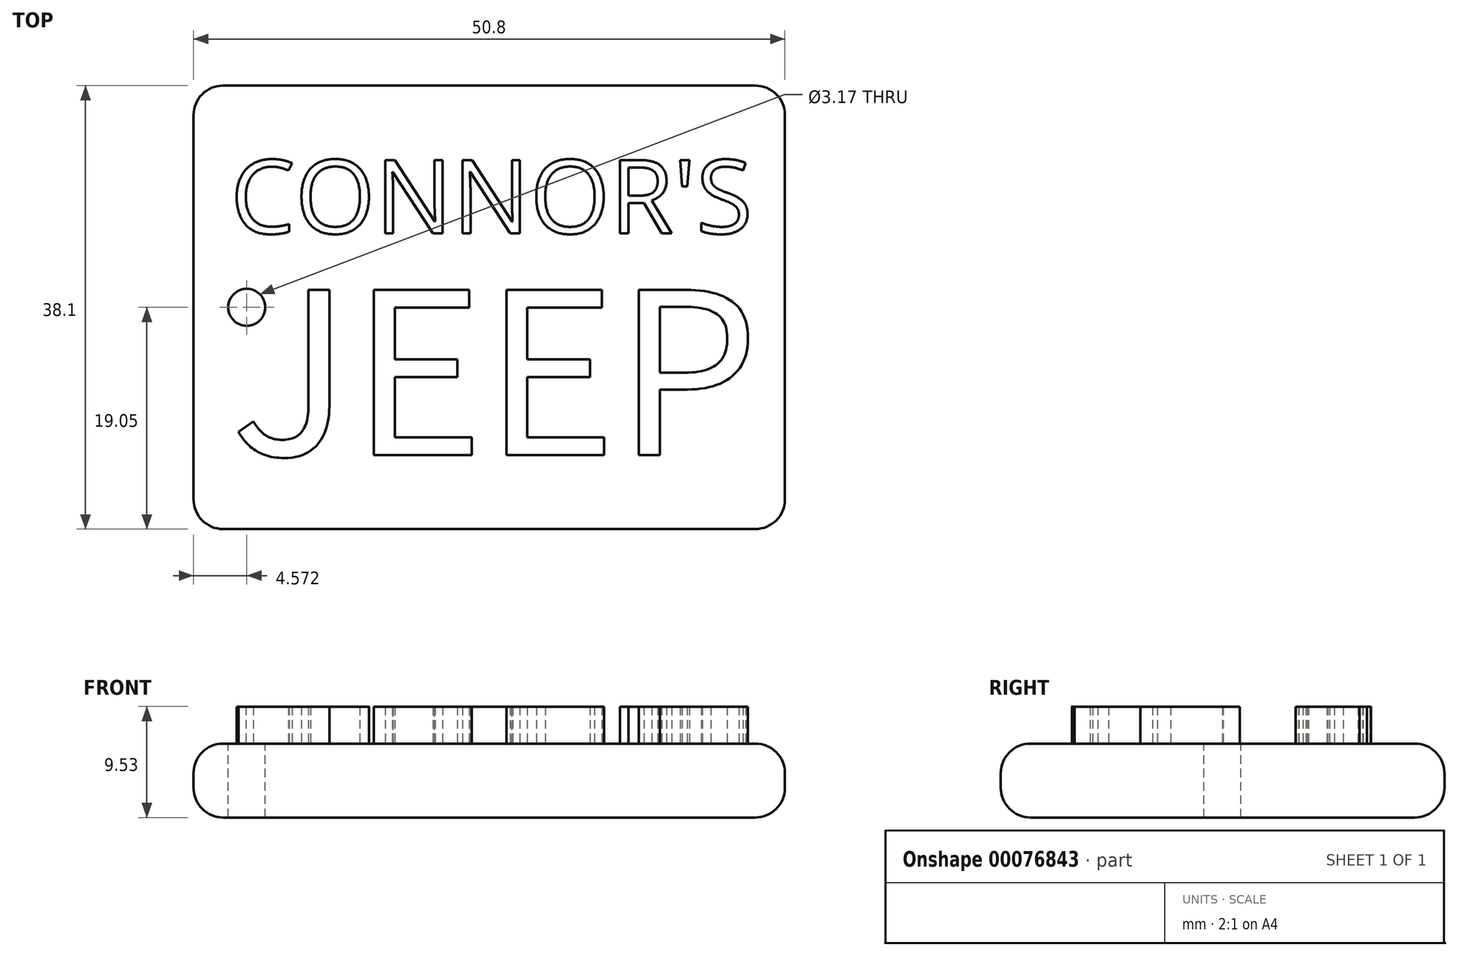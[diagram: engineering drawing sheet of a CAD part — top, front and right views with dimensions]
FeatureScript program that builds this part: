
annotation { "Feature Type Name" : "Feature", "Feature Type Description" : "" }
export const myFeature = defineFeature(function(context is Context, id is Id, definition is map)
    precondition{}
    {
        {
            var Q0;
            Q0=qCreatedBy(makeId("Top.planeOp"),FACE);
            var sketch = newSketch(context, id + "F0", { "sketchPlane" : qUnion([Q0])});
            skLineSegment(sketch, "E0.bottom", {"start": v(-31.75, 25.4) * mm, "end": v(19.05, 25.4) * mm});
            skLineSegment(sketch, "E0.top", {"start": v(-31.75, -12.7) * mm, "end": v(19.05, -12.7) * mm});
            skLineSegment(sketch, "E0.left", {"start": v(-31.75, 25.4) * mm, "end": v(-31.75, -12.7) * mm});
            skLineSegment(sketch, "E0.right", {"start": v(19.05, 25.4) * mm, "end": v(19.05, -12.7) * mm});
            skSolve(sketch);
        }
        {
            var Q0;
            Q0 = qSketchRegion(id + "F0", true);
            extrude(context, id + "F1", {"entities" : qUnion([Q0]), "depth" : 6.35 * mm});
        }
        {
            var Q0;
            Q0=makeQuery(id+"F1.opExtrude","CAP_FACE",FACE,{"disambiguationData":[OSD([sQuery(id+"F0.wireOp",EDGE,"E0.bottom"),sQuery(id+"F0.wireOp",EDGE,"E0.top"),sQuery(id+"F0.wireOp",EDGE,"E0.left"),sQuery(id+"F0.wireOp",EDGE,"E0.right")])],"isStart":false});
            var sketch = newSketch(context, id + "F2", { "sketchPlane" : qUnion([Q0])});
            skText(sketch, "E1", { "text": "JEEP", "fontName": "NotoSansCJKtc-Regular.otf"});
            const initialGuessF2  = {"E1": [-0.02857, -0.00635, 1, 0, 0.01394]};
            skSetInitialGuess(sketch, initialGuessF2);
            skSolve(sketch);
        }
        {
            var Q0;
            Q0 = qSketchRegion(id + "F2", true);
            extrude(context, id + "F3", {"entities" : qUnion([Q0]), "operationType" : NewBodyOperationType.ADD, "depth" : 3.17 * mm});
        }
        {
            var Q0;
            {var subQ0=sQuery(id+"F0.wireOp",EDGE,"E0.bottom");var subQ1=sQuery(id+"F0.wireOp",EDGE,"E0.right");var subQ2=sQuery(id+"F0.wireOp",EDGE,"E0.top");var subQ3=sQuery(id+"F0.wireOp",EDGE,"E0.left");Q0=makeQuery(id+"F3.boolean.opBoolean","SPLIT",FACE,{"disambiguationData":[TD([makeQuery(id+"F1.opExtrude","SWEPT_FACE",FACE,{"disambiguationData":[OSD([subQ0])]})])],"derivedFrom":makeQuery(id+"F1.opExtrude","CAP_FACE",FACE,{"disambiguationData":[OSD([subQ0,subQ2,subQ3,subQ1])],"isStart":false})});}
            var sketch = newSketch(context, id + "F4", { "sketchPlane" : qUnion([Q0])});
            skText(sketch, "E2", { "text": "CONNOR\'S\n", "fontName": "OpenSans-Regular.ttf"});
            const initialGuessF4  = {"E2": [-0.02858, 0.0127, 1, 0, 0.00635]};
            skSetInitialGuess(sketch, initialGuessF4);
            skSolve(sketch);
        }
        {
            var Q0;
            Q0 = qSketchRegion(id + "F4", true);
            extrude(context, id + "F5", {"entities" : qUnion([Q0]), "operationType" : NewBodyOperationType.ADD, "depth" : 3.17 * mm});
        }
        {
            var Q0;
            {var subQ2=sQuery(id+"F0.wireOp",EDGE,"E0.left");var subQ17=sQuery(id+"F0.wireOp",EDGE,"E0.bottom");var subQ18=makeQuery(id+"F1.opExtrude","SWEPT_FACE",FACE,{"disambiguationData":[OSD([subQ17])]});var subQ19=sQuery(id+"F0.wireOp",EDGE,"E0.right");var subQ21=sQuery(id+"F0.wireOp",EDGE,"E0.top");Q0=makeQuery(id+"F5.boolean.opBoolean","SPLIT",FACE,{"disambiguationData":[TD([subQ18])],"derivedFrom":makeQuery(id+"F3.boolean.opBoolean","SPLIT",FACE,{"disambiguationData":[TD([subQ18])],"derivedFrom":makeQuery(id+"F1.opExtrude","CAP_FACE",FACE,{"disambiguationData":[OSD([subQ17,subQ21,subQ2,subQ19])],"isStart":false})})});}
            var sketch = newSketch(context, id + "F6", { "sketchPlane" : qUnion([Q0])});
            skLineSegment(sketch, "E3", {"start": v(-27.18, -12.7) * mm, "end": v(-27.18, 25.4) * mm, "construction": true});
            skLineSegment(sketch, "E4", {"start": v(-31.75, 6.35) * mm, "end": v(19.05, 6.35) * mm, "construction": true});
            skCircle(sketch, "E5", {"center": v(-27.18, 6.35) * mm, "radius": 1.59 * mm});
            skSolve(sketch);
        }
        {
            var Q0;
            Q0 = qSketchRegion(id + "F6", true);
            extrude(context, id + "F7", {"entities" : qUnion([Q0]), "operationType" : NewBodyOperationType.REMOVE, "oppositeDirection" : true, "depth" : 25.4 * mm});
        }
        {
            var Q0;
            Q0=makeQuery(id+"F1.opExtrude","CAP_EDGE",EDGE,{"disambiguationData":[OSD([sQuery(id+"F0.wireOp",EDGE,"E0.top")])],"isStart":false});
            var Q1;
            Q1=makeQuery(id+"F1.opExtrude","CAP_EDGE",EDGE,{"disambiguationData":[OSD([sQuery(id+"F0.wireOp",EDGE,"E0.top")])],"isStart":true});
            var Q2;
            Q2=makeQuery(id+"F1.opExtrude","CAP_EDGE",EDGE,{"disambiguationData":[OSD([sQuery(id+"F0.wireOp",EDGE,"E0.right")])],"isStart":false});
            var Q3;
            Q3=makeQuery(id+"F1.opExtrude","CAP_EDGE",EDGE,{"disambiguationData":[OSD([sQuery(id+"F0.wireOp",EDGE,"E0.right")])],"isStart":true});
            var Q4;
            Q4=makeQuery(id+"F1.opExtrude","SWEPT_EDGE",EDGE,{"disambiguationData":[OSD([sQuery(id+"F0.wireOp",EDGE,"E0.top"),sQuery(id+"F0.wireOp",EDGE,"E0.right")])]});
            var Q5;
            Q5=makeQuery(id+"F1.opExtrude","CAP_EDGE",EDGE,{"disambiguationData":[OSD([sQuery(id+"F0.wireOp",EDGE,"E0.bottom")])],"isStart":true});
            var Q6;
            Q6=makeQuery(id+"F1.opExtrude","SWEPT_EDGE",EDGE,{"disambiguationData":[OSD([sQuery(id+"F0.wireOp",EDGE,"E0.bottom"),sQuery(id+"F0.wireOp",EDGE,"E0.right")])]});
            var Q7;
            Q7=makeQuery(id+"F1.opExtrude","CAP_EDGE",EDGE,{"disambiguationData":[OSD([sQuery(id+"F0.wireOp",EDGE,"E0.bottom")])],"isStart":false});
            var Q8;
            Q8=makeQuery(id+"F1.opExtrude","CAP_EDGE",EDGE,{"disambiguationData":[OSD([sQuery(id+"F0.wireOp",EDGE,"E0.left")])],"isStart":true});
            var Q9;
            Q9=makeQuery(id+"F1.opExtrude","SWEPT_EDGE",EDGE,{"disambiguationData":[OSD([sQuery(id+"F0.wireOp",EDGE,"E0.bottom"),sQuery(id+"F0.wireOp",EDGE,"E0.left")])]});
            var Q10;
            Q10=makeQuery(id+"F1.opExtrude","SWEPT_EDGE",EDGE,{"disambiguationData":[OSD([sQuery(id+"F0.wireOp",EDGE,"E0.top"),sQuery(id+"F0.wireOp",EDGE,"E0.left")])]});
            var Q11;
            Q11=makeQuery(id+"F1.opExtrude","CAP_EDGE",EDGE,{"disambiguationData":[OSD([sQuery(id+"F0.wireOp",EDGE,"E0.left")])],"isStart":false});
            fillet(context, id + "F8", {"entities" : qUnion([Q0, Q1, Q2, Q3, Q4, Q5, Q6, Q7, Q8, Q9, Q10, Q11]), "radius" : 2.54 * mm, "tangentPropagation" : true, "allowEdgeOverflow" : false});
        }
    });
